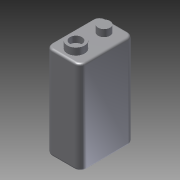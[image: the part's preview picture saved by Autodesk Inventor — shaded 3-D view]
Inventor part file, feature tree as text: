
AUTODESK INVENTOR PART (.ipt)
format: ipt  version: 2011 SP2 (Build 150309200, 309)  size: 133,632 bytes
history: native  units: mm
features: extrude x3, sketch x3, fillet x2
ambient origin geometry x8: Origin, YZ Plane, XZ Plane, XY Plane, X Axis, Y Axis, Z Axis, Center Point
bodies: Solid1 (feature_tree)
feature tree (8):
  extrude  "Extrusion1"  Depth=44.3mm
  extrude  "Extrusion2"  Depth=8.3mm
  extrude  "Extrusion3"  Depth=13.4mm
  fillet  "Fillet1"  Radius=6.15mm
  fillet  "Fillet2"  Radius=3.3mm
  sketch  "Sketch1"  dims[d0=25.7mm d1=44.3mm]
  sketch  "Sketch2"  dims[d2=16.6mm d3=0.0mm d4=8.3mm]
  sketch  "Sketch3"  dims[d5=5.7mm d6=13.4mm d7=6.15mm d8=3.3mm d9=0.0mm d10=5.7mm d11=3.0mm d12=0.0mm d13=3.0mm d14=1.0mm]
